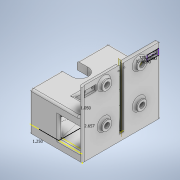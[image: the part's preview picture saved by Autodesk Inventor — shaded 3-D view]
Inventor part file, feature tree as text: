
AUTODESK INVENTOR PART (.ipt)
format: ipt  version: 2020 (Build 240168000, 168)  size: 506,368 bytes
history: native  units: in
note: dims shown in document units (in); Inventor stores cm internally (conversion verified against a paired STEP export)
features: sketch x17, extrude x14, hole x4, plane x1, mirror x1, fillet x1
ambient origin geometry x8: Origin, YZ Plane, XZ Plane, XY Plane, X Axis, Y Axis, Z Axis, Center Point
bodies: Solid1 (feature_tree)
feature tree (38):
  extrude  "Extrusion1"  Depth=5.0299in
  extrude  "Extrusion2"  Depth=0.375in
  extrude  "Extrusion3"  Depth=2.8543in
  sketch  "Sketch5"  dims[d24=5.315in d25=4.5472in]
  extrude  "Extrusion4"  Depth=4.5472in
  extrude  "Extrusion5"  Depth=0.25in
  extrude  "Extrusion6"  Depth=2.6575in
  hole  "Hole2"  [1 undecoded]
  extrude  "Extrusion7"  Depth=0.5in
  extrude  "Extrusion8"  Depth=1.5in
  extrude  "Extrusion9"  Depth=0.312in
  extrude  "Extrusion10"  Depth=0.312in
  hole  "Hole3"  [1 undecoded]
  extrude  "Extrusion11"  Depth=1.5in TaperAngle=0.0deg
  extrude  "Extrusion12"  Depth=1.125in
  hole  "Hole4"  [1 undecoded]
  sketch  "Sketch17"  dims[d61=1.49in d62=2.25in]
  extrude  "Extrusion13"  TaperAngle=90.0deg  [1 undecoded]
  hole  "Hole5"  [1 undecoded]
  plane  "Work Plane1"
  mirror  "Mirror1"
  extrude  "Extrusion14"  TaperAngle=0.0deg  [1 undecoded]
  fillet  "Fillet1"  Radius=0.625in
  sketch  "Sketch18"  dims[d63=2.25in d64=90.0deg]
  sketch  "Sketch1"  dims[d0=3.3654in d1=5.0299in]
  sketch  "Sketch3"  dims[d3=45.0deg d4=0.375in]
  sketch  "Sketch4"  dims[d5=0.5in d6=0.0in d23=2.8543in]
  sketch  "Sketch6"  dims[d26=0.1in d27=0.0in d28=0.25in]
  sketch  "Sketch7"  dims[d29=0.1in d30=0.0in d31=2.6575in]
  sketch  "Sketch9"  dims[d32=1.05in d33=1.25in]
  sketch  "Sketch10"  dims[d34=1.9685in d35=0.0in d36=0.5in]
  sketch  "Sketch11"  dims[d37=5.03in d38=0.0in d39=1.5in]
  sketch  "Sketch12"  dims[d40=1.0in d41=0.0in d42=0.312in]
  sketch  "Sketch13"  dims[d43=0.0in d44=0.312in]
  sketch  "Sketch14"  dims[d45=0.177in d46=0.75in d47=0.385in d48=0.25in d49=0.5635in d50=1.378in d51=0.0in d52=1.9685in d53=0.0in]
  sketch  "Sketch15"  dims[d54=1.9685in d55=0.0in d56=1.5in d57=0.0in]
  sketch  "Sketch16"  dims[d58=3.75in d59=0.0in d60=1.125in]
  sketch  "Sketch19"  dims[d65=2.25in d66=90.0deg d67=0.332in d68=0.375in d69=0.119in d70=0.25in d71=0.5635in d72=0.375in d73=0.0in d74=0.0in d75=0.0in d76=0.625in d77=0.625in d78=0.625in d79=0.625in d80=0.2in d81=0.0in d82=0.21in d83=1.125in d84=0.185in d85=0.37in d86=0.09in d87=0.375in d88=0.119in d89=0.25in d90=0.5635in d91=0.375in d92=0.0in d93=0.375in d94=0.0in d95=0.25in d96=0.5in d97=0.375in d98=0.125in d99=0.0in d100=0.129in d101=0.198in d102=0.225in d103=0.188in d104=0.5635in d105=0.375in d106=0.0in d107=0.125in d108=0.125in d109=1.0in d110=1.0in d111=0.5in d112=1.5in d113=0.0in]
note: 6 required parameter values undecoded (feature->parameter linkage not recoverable at this tier; creation-order binding heuristic only, values carry confidence <= 0.55)
